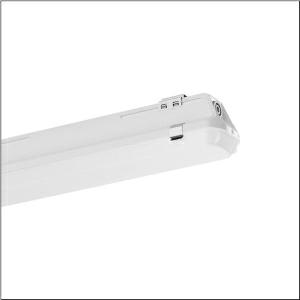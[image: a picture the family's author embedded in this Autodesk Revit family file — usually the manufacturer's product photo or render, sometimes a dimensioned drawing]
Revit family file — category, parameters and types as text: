
# Revit family: monsun_r__21_51fb10dp460b_c90e
name_source: partatom
category: Lighting Fixtures
units: mm (PartAtom-declared; Revit-internal decimal feet)

## family parameters
Cut with Voids When Loaded = No
Host = Face
Light Source = No
Part Type = Normal
Room Calculation Point = No
Round Connector Dimension = Use Diameter
Shared = No

## types (1)
- --- (1 x LED, 6060 lm, 39.4 W, 4000K)
    Apparent Load = 39 VA
    CIE Flux Codes = 47 77 93 94 100
    Color Rendering = 80
    Color Temperature = 4000K
    Default Elevation = 1800 mm
    Description = Monsun® 21, damp-proof luminaire, chain hanger, primary optical cover: enclosure, of PMMA, light emission: direct distribution, primary light characteristic: symmetric, installation type: suspended mounting, surface-mounted, horizontal mounting, vertical mounting, LED, rated luminous flux: 6.060lm, luminous efficacy: 154lm/W, light colour: 840, colour temperature: 4000K, control gear: ECG DALI, with terminal, 5-pole, max. 2.5mm², mains connection: 220..240V, AC, 50/60Hz, rated input power: 39W, housing, of glass-fibre reinforced polyester, uncoated, bright grey, incl. chain hanger, length: 1.590mm, width: 90mm, height: 88mm, clip for enclosure, of stainless steel (V2A), ceiling mounting element, of stainless steel (V2A), chain hanger, of stainless steel (V2A), protection rating (complete): IP66, insulation class (complete): insulation class I (protective earthing), certification: CE, ENEC, VDE, UKCA, protection symbol: D, impact resistance: IK04, permissible operating ambient temperature: -25..+35°C, standard: EN 50419, EN 60598-2-1, corresponds to IFS (International Featured Standards) requirements for safety and quality in the food industry, for indoor or canopied outdoor use, no direct snow, no direct sun, no direct rain, contact your sales advisor before using the luminaires in applications with unclear chemical exposure, large temperature fluctuations or condensation-forming humidity, LABS conformity tested according to VDMA 24364:2018-05, packaging unit: 1 piece
    Height = 89 mm
    Lamp = 1 x LED
    Lamp Light Flux = 6060 lm
    Lamp Power = 39.4 W
    Lamp count = 1
    Length = 1590 mm
    Luminous efficacy = 154 lm/W
    Manufacturer = Siteco
    ModVariant = No
    Model = 51FB10DP460B
    Mounting Place = Ceiling
    Mounting Type = Surface mounted
    Number of Poles = 1
    OnlyDefault = Yes
    Power Factor = 1
    Product Name = Monsun® 21
    Product group = damp-proof luminaire
    ProductGroupID = 301
    Protection Class = Protection class I
    Protection Degree = IP 66
    RLX_Detail_Level = 1
    RLX_Emergency_Light_Flux = 0 lm
    RLX_Emergency_Type = 0
    RLX_Emergency_Type_DB = No
    RlxData = <blob elided: 91861 chars, md5=cda33d5a>
    Socket = socket
    Standby Power = 0 W
    System Light Flux = 6060 lm
    System Power = 39 W
    Type Comments = factory setting: luminous flux: 100 % | dim-lin: 254 | 261 mA
    Type Image = l_1006717.jpg
    URL = http://relux.com
    VarID = @adj_152373
    Voltage = 0 V
    Weight = 0.00 kg
    Width = 90 mm

## geometry (parser evidence)
native form markers: Blend x4, Sweep x15
no freeform markers — native parametric forms only
